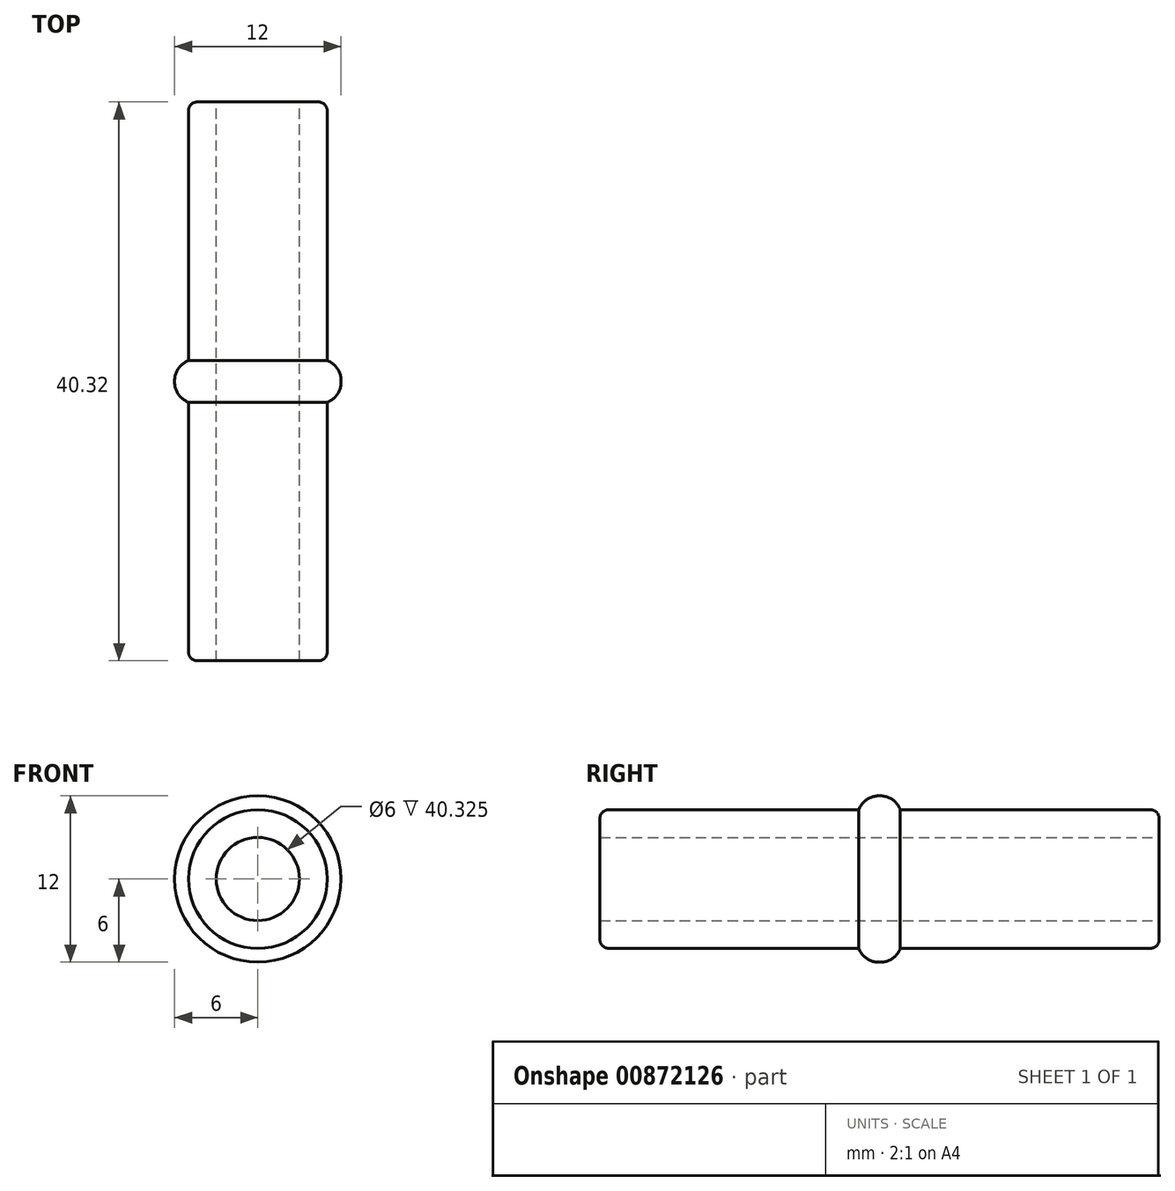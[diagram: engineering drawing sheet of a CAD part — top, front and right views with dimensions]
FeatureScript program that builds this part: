
annotation { "Feature Type Name" : "Feature", "Feature Type Description" : "" }
export const myFeature = defineFeature(function(context is Context, id is Id, definition is map)
    precondition{}
    {
        {
            var Q0;
            Q0=qCreatedBy(makeId("Front.planeOp"),FACE);
            var sketch = newSketch(context, id + "F0", { "sketchPlane" : qUnion([Q0])});
            skCircle(sketch, "E0", {"center": v(0, 0) * mm, "radius": 5 * mm});
            skCircle(sketch, "E1", {"center": v(0, 0) * mm, "radius": 3 * mm});
            skCircle(sketch, "E2", {"center": v(0, 0) * mm, "radius": 6 * mm});
            skSolve(sketch);
        }
        {
            var Q0;
            Q0=makeQuery(id+"F0.imprint","IMPRINT",FACE,{"disambiguationData":[TD([[makeQuery(id+"F0.imprint","IMPRINT",EDGE,{"derivedFrom":sQuery(id+"F0.wireOp",EDGE,"E0")}),1.0]])]});
            extrude(context, id + "F1", {"entities" : qUnion([Q0]), "endBound" : BoundingType.SYMMETRIC, "depth" : 40.32 * mm, "offsetDistance" : 25.4 * mm});
        }
        {
            var Q0;
            Q0=makeQuery(id+"F1.opExtrude","CAP_EDGE",EDGE,{"disambiguationData":[OSD([sQuery(id+"F0.wireOp",EDGE,"E0")])],"isStart":false});
            var Q1;
            Q1=makeQuery(id+"F1.opExtrude","CAP_EDGE",EDGE,{"disambiguationData":[OSD([sQuery(id+"F0.wireOp",EDGE,"E0")])],"isStart":true});
            fillet(context, id + "F2", {"entities" : qUnion([Q0, Q1]), "radius" : 0.63 * mm, "tangentPropagation" : true, "allowEdgeOverflow" : false});
        }
        {
            var Q0;
            Q0 = qSketchRegion(id + "F0", true);
            extrude(context, id + "F3", {"entities" : qUnion([Q0]), "operationType" : NewBodyOperationType.ADD, "endBound" : BoundingType.SYMMETRIC, "depth" : 3 * mm, "offsetDistance" : 25 * mm});
        }
        {
            var Q0;
            Q0=makeQuery(id+"F3.opExtrude","CAP_EDGE",EDGE,{"disambiguationData":[OSD([sQuery(id+"F0.wireOp",EDGE,"E2")])],"isStart":true});
            var Q1;
            Q1=makeQuery(id+"F3.opExtrude","CAP_EDGE",EDGE,{"disambiguationData":[OSD([sQuery(id+"F0.wireOp",EDGE,"E2")])],"isStart":false});
            fillet(context, id + "F4", {"entities" : qUnion([Q0, Q1]), "radius" : 1.52 * mm, "tangentPropagation" : true, "allowEdgeOverflow" : false});
        }
    });
